# Revit family: Toilet_Elongated-One_Piece-American_Standard-Champion-2004.314
name_source: partatom
category: Plumbing Fixtures
revit_build: Autodesk Revit 2014 (Build: 20130308_1515(x64)
units: mm (PartAtom-declared; Revit-internal decimal feet)

## types (1)
- 2004.314
    Assembly Code = D2010110
    Bowl Shape = Elongated
    CW Connection = Yes
    CWFU = 5
    Cold Water Connection Diameter = 3/8"
    Cold Water Connection Height = 4 1/2"
    Cold Water Connection Radius = 3/16"
    Cold Water Connection Width = 7"
    Default Elevation = 15"
    Description = American Standard Champion 4 Elongated One-Piece Toilet Seat Included.
    Flush Rate = 6.0 Lpf (1.6 gpf)
    HW Connection = No
    HWFU = 0
    Height = 28 1/8"
    Installation Type = Floor Mounted
    Length = 29 3/4"
    Manufacturer = American Standard
    Material = Vitreous China-American Standard-020-White
    Model = 2004.314
    Price = Prices may vary. Please consult Manufacturer Representative for most up-to-date price list.
    Product Documentation Link = https://www.americanstandard-us.com
    Product Page URL = https://www.americanstandard-us.com
    Type Comments = Slow Close Seat Elongated #5325.010
    URL = http://www.americanstandard-us.com
    Vent Connection = No
    WFU = 5
    Warranty Information = 10 Years
    Waste Connection = Yes
    Waste Connection Diameter = 2 1/8"
    Waste Connection Radius = 1 1/16"
    Width = 17 3/4"

## geometry (parser evidence)
native form markers: Sweep x2
no freeform markers — native parametric forms only
